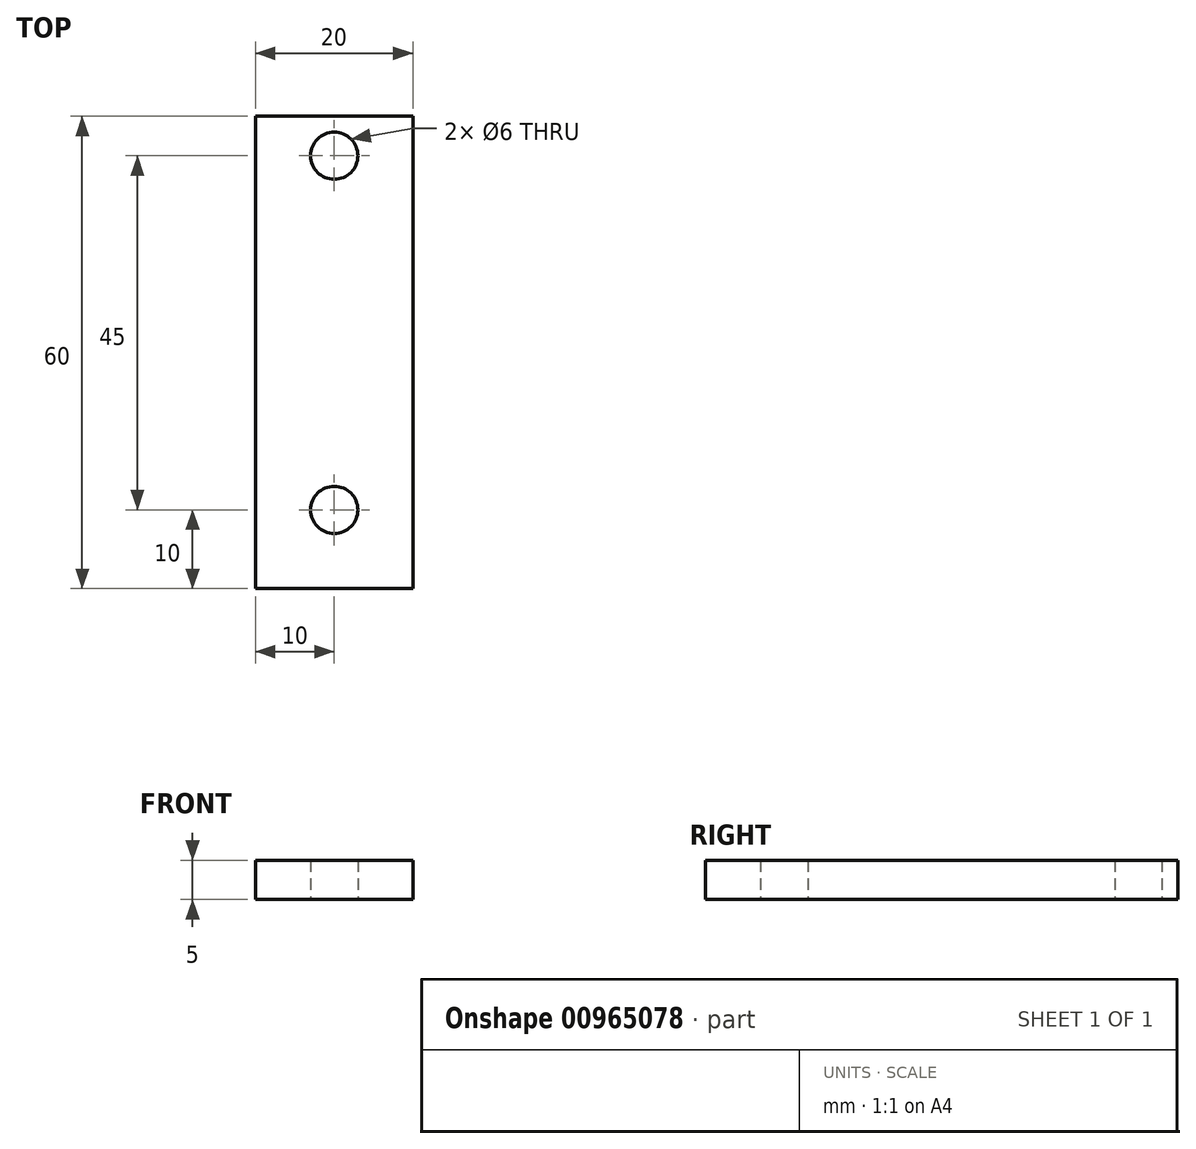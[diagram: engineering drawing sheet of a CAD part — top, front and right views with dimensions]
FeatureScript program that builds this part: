
annotation { "Feature Type Name" : "Feature", "Feature Type Description" : "" }
export const myFeature = defineFeature(function(context is Context, id is Id, definition is map)
    precondition{}
    {
        {
            var Q0;
            Q0=qCreatedBy(makeId("Top.planeOp"),FACE);
            var sketch = newSketch(context, id + "F0", { "sketchPlane" : qUnion([Q0])});
            skLineSegment(sketch, "E0.bottom", {"start": v(0, 0) * mm, "end": v(20, 0) * mm});
            skLineSegment(sketch, "E0.top", {"start": v(0, 60) * mm, "end": v(20, 60) * mm});
            skLineSegment(sketch, "E0.left", {"start": v(0, 0) * mm, "end": v(0, 60) * mm});
            skLineSegment(sketch, "E0.right", {"start": v(20, 0) * mm, "end": v(20, 60) * mm});
            skCircle(sketch, "E1", {"center": v(10, 55) * mm, "radius": 3 * mm});
            skCircle(sketch, "E2", {"center": v(10, 10) * mm, "radius": 3 * mm});
            skSolve(sketch);
        }
        {
            var Q0;
            Q0=makeQuery(id+"F0.imprint","IMPRINT",FACE,{"disambiguationData":[TD([[makeQuery(id+"F0.imprint","IMPRINT",EDGE,{"derivedFrom":sQuery(id+"F0.wireOp",EDGE,"E0.bottom")}),1.0]])]});
            extrude(context, id + "F1", {"entities" : qUnion([Q0]), "depth" : 5 * mm, "offsetDistance" : 25 * mm});
        }
    });
